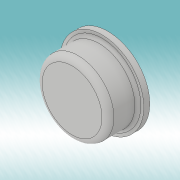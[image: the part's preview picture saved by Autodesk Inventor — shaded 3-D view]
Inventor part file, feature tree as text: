
AUTODESK INVENTOR PART (.ipt)
format: ipt  version: 2019 (Build 230136000, 136)  size: 148,992 bytes
history: native  units: mm
features: extrude x2, sketch x2, fillet x1
ambient origin geometry x8: Origin, YZ Plane, XZ Plane, XY Plane, X Axis, Y Axis, Z Axis, Center Point
bodies: Body1 (feature_tree)
feature tree (5):
  extrude  "Extrusion2"  Depth=8.0mm
  extrude  "Extrusion3"  Depth=0.5mm
  fillet  "Fillet1"  Radius=1.0mm
  sketch  "Sketch1"  dims[d0=16.0mm d1=8.0mm]
  sketch  "Sketch3"  dims[d2=8.0mm d3=14.0mm d7=1.0mm d8=0.0mm d10=12.0mm d11=5.0mm d12=0.0mm d13=1.0mm d14=0.5mm]
